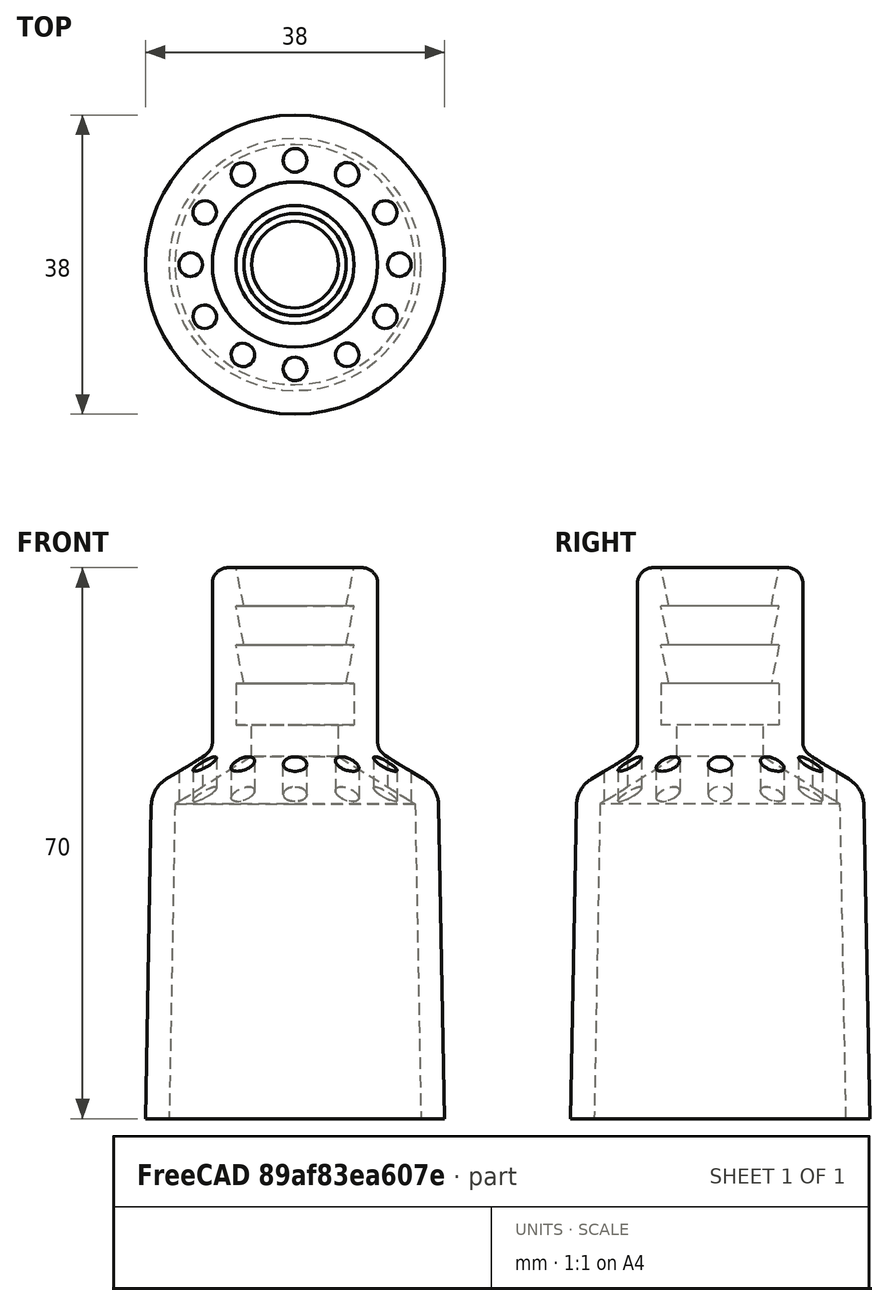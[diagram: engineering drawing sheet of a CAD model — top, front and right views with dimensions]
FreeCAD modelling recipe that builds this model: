
FCSTD DOCUMENT  (FreeCAD 1.1R20260414 (Git shallow))
Label: VacAdapter
License: All rights reserved
LicenseURL: http://en.wikipedia.org/wiki/All_rights_reserved
objects: PartDesign::Fillet×3, App::Point×2, Sketcher::SketchObject×2, Spreadsheet::Sheet×1, PartDesign::Revolution×1, PartDesign::Pocket×1, PartDesign::PolarPattern×1, PartDesign::Body×1, App::Part×1, Mesh::Feature×1
note: 22 computed .brp shape members not serialized (recipe doc carries the construction recipe); baked Part::Feature solids carry a one-line shape summary decoded from their .brp

FEATURE [App::Point] Origin001
  Role = Origin
FEATURE [App::Point] Origin003
  Role = Origin
FEATURE [Sketcher::SketchObject] Sketch  label="Sketch-Body"
  ArcFitTolerance = 1e-06
  AttachmentSupport = -> [Origin002]
  ExternalTypes = [0]
  FullyConstrained = true
  MakeInternals = false
  MapMode = 5
  Placement = pos=(0,0,0) rot=(0.57735,0.57735,0.57735;2.0944rad)
  _ExternalGeoVersion = 1
  expr: Constraints[16] = Spreadsheet.Neck / 2
  expr: Constraints[17] = Spreadsheet.Thick
  expr: Constraints[18] = Spreadsheet.Neck / 2
  expr: Constraints[19] = Spreadsheet.Spike
  expr: Constraints[28] = Spreadsheet.Neck / 2
  expr: Constraints[29] = Spreadsheet.Spike * 2
  expr: Constraints[40] = Spreadsheet.Length
  expr: Constraints[41] = Spreadsheet.Neck / 2
  expr: Constraints[44] = Spreadsheet.Seperation + 6
  expr: Constraints[4] = Spreadsheet.Wall
  expr: Constraints[5] = Spreadsheet.Seperation + 2
  expr: Constraints[6] = Spreadsheet.BottomDiam / 2
  expr: Constraints[7] = Spreadsheet.Seperation
  expr: Constraints[8] = Spreadsheet.TopDiam / 2
  sketch-geometry (16):
    g0: LineSegment StartX=16 StartY=0 StartZ=0 EndX=15.25 EndY=40 EndZ=0
    g1: LineSegment StartX=16 StartY=0 StartZ=0 EndX=19 EndY=0 EndZ=0
    g2: LineSegment StartX=19 StartY=0 StartZ=0 EndX=18.2125 EndY=42 EndZ=0
    g3: LineSegment StartX=10.5 StartY=46.7462 StartZ=0 EndX=10.5 EndY=70 EndZ=0
    g4: LineSegment StartX=6.5 StartY=60.202 StartZ=0 EndX=7.5 EndY=65.101 EndZ=0
    g5: LineSegment StartX=7.5 StartY=65.101 StartZ=0 EndX=6.5 EndY=65.101 EndZ=0
    g6: LineSegment StartX=6.5 StartY=65.101 StartZ=0 EndX=7.5 EndY=70 EndZ=0
    g7: LineSegment StartX=7.5 StartY=70 StartZ=0 EndX=10.5 EndY=70 EndZ=0
    g8: LineSegment StartX=6.5 StartY=60.202 StartZ=0 EndX=7.5 EndY=60.202 EndZ=0
    g9: LineSegment StartX=5.5 StartY=46 StartZ=0 EndX=15.25 EndY=40 EndZ=0
    g10: LineSegment StartX=5.5 StartY=46 StartZ=0 EndX=5.5 EndY=50 EndZ=0
    g11: LineSegment StartX=5.5 StartY=50 StartZ=0 EndX=7.5 EndY=50 EndZ=0
    g12: LineSegment StartX=7.5 StartY=60.202 StartZ=0 EndX=6.5 EndY=55.3031 EndZ=0
    g13: LineSegment StartX=6.5 StartY=55.3031 StartZ=0 EndX=7.5 EndY=55.3031 EndZ=0
    g14: LineSegment StartX=7.5 StartY=55.3031 StartZ=0 EndX=7.5 EndY=50 EndZ=0
    g15: LineSegment StartX=10.5 StartY=46.7462 StartZ=0 EndX=18.2125 EndY=42 EndZ=0
  constraints (48):
    c: PointOnObject(g0,g-1)
    c: Coincident(g1,g0)
    c: PointOnObject(g1,g-1)
    c: Coincident(g2,g1)
    c: DistanceX(g1,g1) = 3
    c: DistanceY(g2,g2) = 42
    c: DistanceX(g-1,g0) = 16
    c: DistanceY(g0,g0) = 40
    c: DistanceX(g-1,g0) = 15.25
    c: Parallel(g0,g2)
    c: Vertical(g3)
    c: Horizontal(g5)
    c: Coincident(g7,g3)
    c: Coincident(g5,g6)
    c: Coincident(g5,g4)
    c: Coincident(g6,g7)
    c: DistanceX(g-1,g6) = 7.5
    c: DistanceX(g7,g7) = 3
    c: DistanceX(g-1,g4) = 7.5
    c: DistanceX(g5,g5) = 1
    c: Horizontal(g7)
    c: Coincident(g8,g4)
    c: Equal(g8,g5)
    c: Coincident(g10,g9)
    c: Vertical(g10)
    c: Coincident(g11,g10)
    c: Horizontal(g11)
    c: Horizontal(g8)
    c: DistanceX(g-1,g8) = 7.5
    c: DistanceX(g11,g11) = 2
    c: Coincident(g12,g8)
    c: Coincident(g13,g12)
    c: Horizontal(g13)
    c: Coincident(g14,g13)
    c: Coincident(g14,g11)
    c: Vertical(g14)
    c: Equal(g13,g8)
    c: Distance(g10) = 4
    c: Coincident(g15,g3)
    c: Coincident(g15,g2)
    c: DistanceY(g10,g6) = 20
    c: DistanceX(g-1,g13) = 7.5
    c: Parallel(g9,g15)
    c: Coincident(g0,g9)
    c: DistanceY(g-1,g9) = 46
    c: Distance(g6) = 5
    c: Equal(g6,g4)
    c: Equal(g4,g12)
FEATURE [Spreadsheet::Sheet] Spreadsheet
  cells = A1='TopDiam; B1(TopDiam)=30.5; C1='mm; A2='BottomDiam; B2(BottomDiam)=32; C2='mm; A3='Seperation; B3(Seperation)=40; C3='mm; A4='Wall; B4(Wall)=3; C4='mm; A6='Neck; B6(Neck)=15; C6='mm; A7='Length; B7(Length)=20; C7='mm; A8='Spike; B8(Spike)=1; C8='mm; A9='Thick; B9(Thick)=3; C9='mm
FEATURE [PartDesign::Revolution] Revolution
  Angle = 360
  Angle2 = 0
  Axis = (0,0,1)
  Base = (0,0,0)
  FuseOrder = 0
  Profile = -> Sketch
  ReferenceAxis = -> Sketch [V_Axis]
  Reversed = true
  Suppressed = false
  Type = 0
FEATURE [Sketcher::SketchObject] Sketch001  label="Sketch-Holes"
  ArcFitTolerance = 1e-06
  AttachmentSupport = -> [Origin002]
  ExternalTypes = [0]
  FullyConstrained = true
  MakeInternals = false
  MapMode = 5
  _ExternalGeoVersion = 1
  expr: Constraints[2] = Spreadsheet.TopDiam / 2 - 2
  sketch-geometry (1):
    g0: Circle CenterX=0 CenterY=13.25 CenterZ=0 NormalX=0 NormalY=0 NormalZ=1 AngleXU=0 Radius=1.5
  constraints (3):
    c: PointOnObject(g0,g-2)
    c: Diameter(g0) = 3
    c: DistanceY(g-1,g0) = 13.25
FEATURE [PartDesign::Pocket] Pocket
  BaseFeature = -> Revolution
  Direction = (0,0,-1)
  Length = 5
  Length2 = 5
  Profile = -> Sketch001
  ReferenceAxis = -> Sketch001 [N_Axis]
  SideType = 2
  Suppressed = false
  Type = 1
  Type2 = 0
FEATURE [PartDesign::PolarPattern] PolarPattern
  Angle = 360
  Axis = -> Sketch001 [N_Axis]
  BaseFeature = -> Pocket
  Mode = 0
  Occurrences = 12
  Offset = 120
  Originals = -> [Pocket]
  SpacingPattern = [0]
  Spacings = [-1,-1,-1,-1,-1,-1,-1,-1,-1,-1,-1]
  Suppressed = false
  TransformMode = 0
FEATURE [PartDesign::Fillet] Fillet
  Base = -> PolarPattern [Edge6]
  BaseFeature = -> PolarPattern
  Radius = 4
  SupportTransform = false
  Suppressed = false
  UseAllEdges = false
FEATURE [PartDesign::Fillet] Fillet001
  Base = -> Fillet [Edge7]
  BaseFeature = -> Fillet
  Radius = 2
  SupportTransform = false
  Suppressed = false
  UseAllEdges = false
FEATURE [PartDesign::Fillet] Fillet002
  Base = -> Fillet001 [Edge50]
  BaseFeature = -> Fillet001
  Radius = 2
  SupportTransform = false
  Suppressed = false
  UseAllEdges = false
FEATURE [PartDesign::Body] Body
  AllowCompound = true
  Group = -> [Sketch,Revolution,Sketch001,Pocket,PolarPattern,Fillet,Fillet001,Fillet002]
  Origin = -> Origin002
  Tip = -> Fillet002
FEATURE [App::Part] Part
  Group = -> [Body]
  Origin = -> Origin
FEATURE [Mesh::Feature] Mesh  label="Fillet002 (Meshed)"
